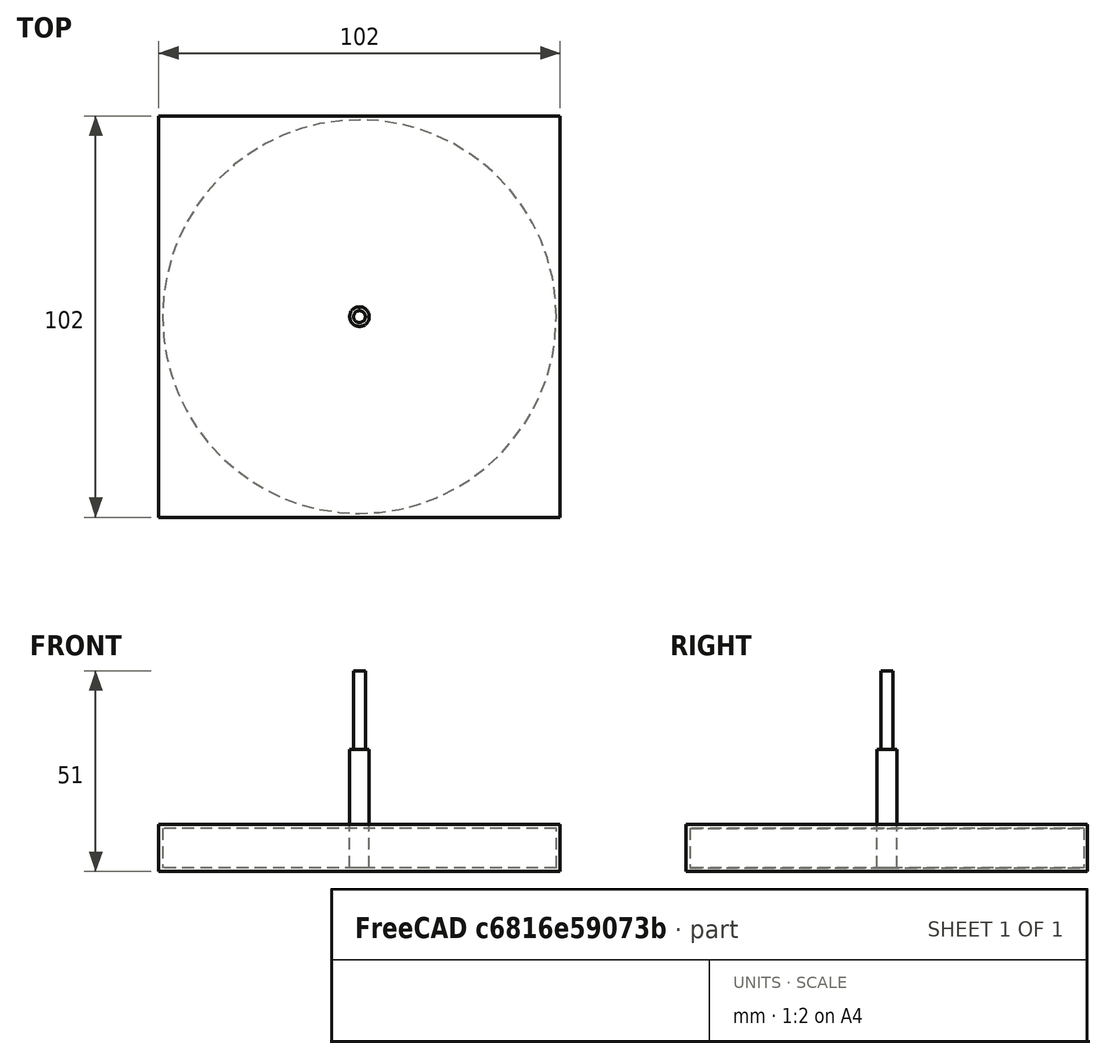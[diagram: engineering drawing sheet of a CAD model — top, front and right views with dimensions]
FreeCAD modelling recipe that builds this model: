
FCSTD DOCUMENT  (FreeCAD 0.19R14555 (Git shallow))
Label: CalibrationPiece
License: All rights reserved
LicenseURL: http://en.wikipedia.org/wiki/All_rights_reserved
objects: Part::FeaturePython×4, Path::FeaturePython×3, App::DocumentObjectGroup×2, Mesh::FeaturePython×2, Sketcher::SketchObject×1, PartDesign::Pad×1, PartDesign::Body×1, App::FeaturePython×1, Path::FeatureCompoundPython×1
note: 9 computed .brp shape members not serialized (recipe doc carries the construction recipe); baked Part::Feature solids carry a one-line shape summary decoded from their .brp

FEATURE [Sketcher::SketchObject] Sketch
  FullyConstrained = true
  MapMode = 5
  Support = -> [XY_Plane]
  sketch-geometry (1):
    g0: Circle CenterX=0 CenterY=0 CenterZ=0 NormalX=0 NormalY=0 NormalZ=1 AngleXU=0 Radius=50
  constraints (3):
    c: DistanceX(g0,g-1) = 0
    c: Diameter(g0) = 100
    c: DistanceY(g-1,g0) = 0
FEATURE [PartDesign::Pad] Pad
  Direction = (1,1,1)
  Length = 10
  Length2 = 100
  Profile = -> Sketch
  Refine = true
  Type = 0
FEATURE [PartDesign::Body] Body
  Group = -> [Sketch,Pad]
  Origin = -> Origin
  Tip = -> Pad
FEATURE [App::FeaturePython] SetupSheet  # Path/CAM operation (typed FeaturePython)
  ClearanceHeightExpression = OpStockZMax+SetupSheet.ClearanceHeightOffset
  ClearanceHeightOffset = 5
  CoolantMode = 0
  CoolantModes = None | Flood | Mist
  FinalDepthExpression = OpFinalDepth
  HorizRapid = 0
  SafeHeightExpression = OpStockZMax+SetupSheet.SafeHeightOffset
  SafeHeightOffset = 3
  StartDepthExpression = OpStartDepth
  StepDownExpression = OpToolDiameter
  VertRapid = 0
FEATURE [Part::FeaturePython] Clone  label="Model-Body"  # Draft clone (typed FeaturePython)
  AttacherType = Attacher::AttachEngine3D
  Fuse = false
  Objects = -> [Body]
  PathResource = Model
  Scale = (1,1,1)
FEATURE [App::DocumentObjectGroup] Model
  Group = -> [Clone]
FEATURE [Part::FeaturePython] Stock001  # WARN: FeaturePython — macro-defined, semantics opaque (R4)
  Base = -> Model
  ExtXneg = 1
  ExtXpos = 1
  ExtYneg = 1
  ExtYpos = 1
  ExtZneg = 1
  ExtZpos = 1
  Placement = pos=(-50,-50,0) rot=(0,0,1;0rad)
  StockType = FromBase
FEATURE [Part::FeaturePython] ToolBit001  label="5mm Endmill"  # Path/CAM toolbit (typed FeaturePython)
  BitPropertyNames = Chipload | CuttingEdgeHeight | Diameter | Flutes | Length | Material | ShankDiameter
  BitShape = /app/freecad/Mod/Path/Tools/Shape/endmill.fcstd
  Chipload = 0
  CuttingEdgeHeight = 30
  Diameter = 5
  File = <userpath>/Documents/CNCRouter/FreeCAD/Bit/5mm_Endmill.fctb
  Flutes = 0
  Length = 50
  Material = 0
  ShankDiameter = 3
  ShapeName = endmill
FEATURE [Path::FeaturePython] _mm_Endmill  label="5mm Endmill001"  # Path/CAM operation (typed FeaturePython)
  HorizFeed = 5
  HorizRapid = 0
  SpindleDir = 0
  SpindleSpeed = 5000
  Tool = -> ToolBit001
  ToolNumber = 1
  VertFeed = 5
  VertRapid = 0
  expr: HorizRapid = SetupSheet.HorizRapid
  expr: VertRapid = SetupSheet.VertRapid
FEATURE [App::DocumentObjectGroup] Tools
  Group = -> [_mm_Endmill]
FEATURE [Path::FeaturePython] Profile  # Path/CAM operation (typed FeaturePython)
  Active = true
  AreaParams:
    Tolerance = 1e-07
    FitArcs = True
    Simplify = False
    CleanDistance = 0.0
    Accuracy = 0.01
    Unit = 1.0
    MinArcPoints = 4
    MaxArcPoints = 100
    ClipperScale = 10000000.0
    Fill = 0
    Coplanar = 0
    Reorient = True
    Outline = False
    Explode = False
    OpenMode = 0
    Deflection = 0.01
    SubjectFill = 0
    ClipFill = 0
    Offset = 2.5
    ExtraPass = 0
    Stepover = 0.0
    LastStepover = 0.0
    JoinType = 0
    EndType = 0
    MiterLimit = 2.0
    RoundPrecision = 0.0
    PocketMode = 0
    ToolRadius = 1.0
    PocketExtraOffset = 0.0
    PocketStepover = 0.0
    PocketLastStepover = 0.0
    FromCenter = False
    Angle = 45.0
    AngleShift = 0.0
    Shift = 0.0
    Thicken = False
    SectionCount = -1
    Stepdown = 1.0
    SectionOffset = 0.0
    SectionTolerance = 1e-06
    SectionMode = 2
    Project = False
  AttemptInverseAngle = true
  ClearanceHeight = 16
  CoolantMode = None
  CycleTime = 00:04:18
  Direction = 0
  EnableRotation = 0
  FinalDepth = -1
  HandleMultipleFeatures = 0
  InverseAngle = false
  JoinType = 0
  LimitDepthToFace = true
  MiterLimit = 0.1
  OffsetExtra = 0
  OpFinalDepth = -1
  OpStartDepth = 11
  OpStockZMax = 11
  OpStockZMin = -1
  OpToolDiameter = 5
  PathParams = {'orientation': 1, 'feedrate': 5.0, 'feedrate_v': 1.0, 'verbose': True, 'resume_height': 14.0, 'retraction': 16.0, 'return_end': True, 'preamble': False}
  ReverseDirection = false
  SafeHeight = 14
  Side = 0
  StartDepth = 11
  StartPoint = (0,0,0)
  StepDown = 5
  ToolController = -> _mm_Endmill
  UseComp = true
  UseStartPoint = false
  processCircles = false
  processHoles = false
  processPerimeter = true
  expr: ClearanceHeight = OpStockZMax + SetupSheet.ClearanceHeightOffset
  expr: SafeHeight = OpStockZMax + SetupSheet.SafeHeightOffset
  expr: StepDown = OpToolDiameter
  expr: FinalDepth = OpFinalDepth
  expr: StartDepth = OpStartDepth
FEATURE [Path::FeatureCompoundPython] Operations  # Path/CAM operation (typed FeaturePython)
  Group = -> [Profile]
  UsePlacements = false
FEATURE [Path::FeaturePython] Job  # Path/CAM operation (typed FeaturePython)
  CycleTime = 00:04:18
  Fixtures = G54
  GeometryTolerance = 0.01
  LastPostProcessDate = 2021-11-29 11:23:26.238522
  LastPostProcessOutput = <userpath>/Documents/CNCRouter/CalibrationPiece
  Model = -> Model
  Operations = -> Operations
  OrderOutputBy = 0
  PostProcessor = 7
  PostProcessorOutputFile = <userpath>/Documents/CNCRouter/CalibrationPiece
  SetupSheet = -> SetupSheet
  SplitOutput = false
  Stock = -> Stock001
  Tools = -> Tools
FEATURE [Part::FeaturePython] CutTool  # WARN: FeaturePython — macro-defined, semantics opaque (R4)
FEATURE [Mesh::FeaturePython] CutMaterial  # WARN: FeaturePython — macro-defined, semantics opaque (R4)
FEATURE [Mesh::FeaturePython] CutMaterialIn  # WARN: FeaturePython — macro-defined, semantics opaque (R4)
